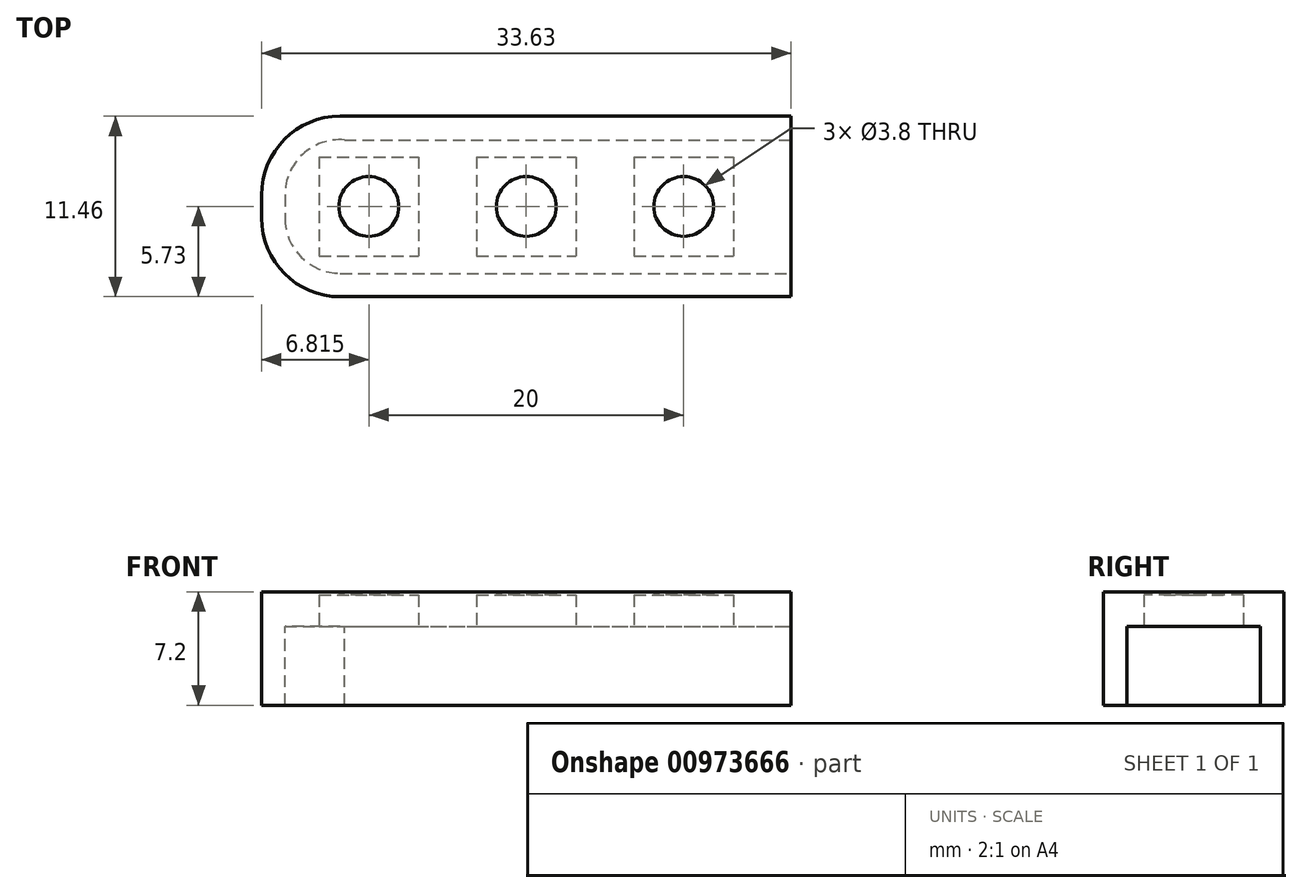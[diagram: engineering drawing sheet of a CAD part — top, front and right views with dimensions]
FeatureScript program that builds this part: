
annotation { "Feature Type Name" : "Feature", "Feature Type Description" : "" }
export const myFeature = defineFeature(function(context is Context, id is Id, definition is map)
    precondition{}
    {
        {
            var Q0;
            Q0=qCreatedBy(makeId("Top.planeOp"),FACE);
            var sketch = newSketch(context, id + "F0", { "sketchPlane" : qUnion([Q0])});
            skLineSegment(sketch, "E0.bottom", {"start": v(-8.24, 3.15) * mm, "end": v(-1.94, 3.15) * mm});
            skLineSegment(sketch, "E0.top", {"start": v(-8.24, -3.15) * mm, "end": v(-1.94, -3.15) * mm});
            skLineSegment(sketch, "E0.left", {"start": v(-8.24, 3.15) * mm, "end": v(-8.24, -3.15) * mm});
            skLineSegment(sketch, "E0.right", {"start": v(-1.94, 3.15) * mm, "end": v(-1.94, -3.15) * mm});
            skPoint(sketch, "E0.middle", {"position": v(-5.09, 0) * mm});
            skLineSegment(sketch, "E1.bottom", {"start": v(1.76, 3.15) * mm, "end": v(8.06, 3.15) * mm});
            skLineSegment(sketch, "E1.top", {"start": v(1.76, -3.15) * mm, "end": v(8.06, -3.15) * mm});
            skLineSegment(sketch, "E1.left", {"start": v(1.76, 3.15) * mm, "end": v(1.76, -3.15) * mm});
            skLineSegment(sketch, "E1.right", {"start": v(8.06, 3.15) * mm, "end": v(8.06, -3.15) * mm});
            skPoint(sketch, "E1.middle", {"position": v(4.91, 0) * mm});
            skLineSegment(sketch, "E2.bottom", {"start": v(11.76, 3.15) * mm, "end": v(18.06, 3.15) * mm});
            skLineSegment(sketch, "E2.top", {"start": v(11.76, -3.15) * mm, "end": v(18.06, -3.15) * mm});
            skLineSegment(sketch, "E2.left", {"start": v(11.76, 3.15) * mm, "end": v(11.76, -3.15) * mm});
            skLineSegment(sketch, "E2.right", {"start": v(18.06, 3.15) * mm, "end": v(18.06, -3.15) * mm});
            skPoint(sketch, "E2.middle", {"position": v(14.91, 0) * mm});
            skLineSegment(sketch, "E3.bottom", {"start": v(-6.9, 5.73) * mm, "end": v(21.73, 5.73) * mm});
            skLineSegment(sketch, "E3.top", {"start": v(-6.9, -5.73) * mm, "end": v(21.73, -5.73) * mm});
            skLineSegment(sketch, "E3.left", {"start": v(-11.9, 0.73) * mm, "end": v(-11.9, -0.73) * mm});
            skLineSegment(sketch, "E3.right", {"start": v(21.73, 5.73) * mm, "end": v(21.73, -5.73) * mm});
            skPoint(sketch, "E4.visualSharp", {"position": v(-11.9, -5.73) * mm});
            skArc(sketch, "E4.filletArc", {"start": v(-11.9, -0.73) * mm, "mid": v(-10.44, -4.27) * mm, "end": v(-6.9, -5.73) * mm});
            skPoint(sketch, "E5.visualSharp", {"position": v(-11.9, 5.73) * mm});
            skArc(sketch, "E5.filletArc", {"start": v(-6.9, 5.73) * mm, "mid": v(-10.44, 4.27) * mm, "end": v(-11.9, 0.73) * mm});
            skSolve(sketch);
        }
        {
            var Q0;
            Q0 = qSketchRegion(id + "F0", true);
            extrude(context, id + "F1", {"entities" : qUnion([Q0]), "depth" : 2 * mm, "offsetDistance" : 25 * mm});
        }
        {
            var Q0;
            Q0=makeQuery(id+"F1.opExtrude","CAP_FACE",FACE,{"disambiguationData":[OSD([sQuery(id+"F0.wireOp",EDGE,"E0.bottom"),sQuery(id+"F0.wireOp",EDGE,"E0.top"),sQuery(id+"F0.wireOp",EDGE,"E0.left"),sQuery(id+"F0.wireOp",EDGE,"E0.right"),sQuery(id+"F0.wireOp",EDGE,"E1.bottom"),sQuery(id+"F0.wireOp",EDGE,"E1.top"),sQuery(id+"F0.wireOp",EDGE,"E1.left"),sQuery(id+"F0.wireOp",EDGE,"E1.right"),sQuery(id+"F0.wireOp",EDGE,"E2.bottom"),sQuery(id+"F0.wireOp",EDGE,"E2.top"),sQuery(id+"F0.wireOp",EDGE,"E2.left"),sQuery(id+"F0.wireOp",EDGE,"E2.right"),sQuery(id+"F0.wireOp",EDGE,"E3.bottom"),sQuery(id+"F0.wireOp",EDGE,"E3.top"),sQuery(id+"F0.wireOp",EDGE,"E3.left"),sQuery(id+"F0.wireOp",EDGE,"E3.right")])],"isStart":true});
            var sketch = newSketch(context, id + "F2", { "sketchPlane" : qUnion([Q0])});
            skLineSegment(sketch, "E6.bottom", {"start": v(-6.9, 5.73) * mm, "end": v(21.73, 5.73) * mm});
            skLineSegment(sketch, "E6.top", {"start": v(-6.9, 4.24) * mm, "end": v(21.73, 4.24) * mm});
            skLineSegment(sketch, "E6.right", {"start": v(21.73, 5.73) * mm, "end": v(21.73, 4.24) * mm});
            skLineSegment(sketch, "E7.bottom", {"start": v(-6.9, -5.73) * mm, "end": v(21.73, -5.73) * mm});
            skLineSegment(sketch, "E7.top", {"start": v(-6.64, -4.23) * mm, "end": v(21.73, -4.23) * mm});
            skLineSegment(sketch, "E7.right", {"start": v(21.73, -5.73) * mm, "end": v(21.73, -4.23) * mm});
            skLineSegment(sketch, "E8.bottom", {"start": v(-6.64, -4.23) * mm, "end": v(-5.4, -4.23) * mm});
            skLineSegment(sketch, "E8.top", {"start": v(-6.9, 4.24) * mm, "end": v(-5.4, 4.24) * mm});
            skArc(sketch, "E9.0", {"start": v(-11.9, 0.73) * mm, "mid": v(-10.44, 4.27) * mm, "end": v(-6.9, 5.73) * mm});
            skLineSegment(sketch, "E9.1", {"start": v(-11.9, -0.73) * mm, "end": v(-11.9, 0.73) * mm});
            skArc(sketch, "E9.2", {"start": v(-6.9, -5.73) * mm, "mid": v(-10.44, -4.27) * mm, "end": v(-11.9, -0.73) * mm});
            skPoint(sketch, "E9.3", {"position": v(-11.9, 0) * mm});
            skArc(sketch, "E10.0", {"start": v(-10.41, 0.73) * mm, "mid": v(-9.39, 3.22) * mm, "end": v(-6.9, 4.24) * mm});
            skLineSegment(sketch, "E10.1", {"start": v(-10.41, -0.73) * mm, "end": v(-10.41, 0.73) * mm});
            skArc(sketch, "E10.2", {"start": v(-6.64, -4.23) * mm, "mid": v(-9.3, -3.3) * mm, "end": v(-10.41, -0.73) * mm});
            skPoint(sketch, "E11", {"position": v(-5.09, 0) * mm});
            skPoint(sketch, "E11.positionSnap0", {"position": v(-5.09, 3.15) * mm});
            skPoint(sketch, "E12", {"position": v(4.91, 0) * mm});
            skPoint(sketch, "E12.positionSnap0", {"position": v(4.91, 3.15) * mm});
            skPoint(sketch, "E12.positionSnap1", {"position": v(8.06, 0) * mm});
            skPoint(sketch, "E13", {"position": v(14.91, 0) * mm});
            skPoint(sketch, "E13.positionSnap0", {"position": v(14.91, 3.15) * mm});
            skSolve(sketch);
        }
        {
            var Q0;
            Q0=makeQuery(id+"F2.imprint","IMPRINT",FACE,{"disambiguationData":[TD([[makeQuery(id+"F2.imprint","IMPRINT",EDGE,{"derivedFrom":sQuery(id+"F2.wireOp",EDGE,"E6.bottom")}),-1.0]])]});
            extrude(context, id + "F3", {"entities" : qUnion([Q0]), "operationType" : NewBodyOperationType.ADD, "depth" : 5 * mm, "offsetDistance" : 25 * mm});
        }
        {
            var Q0;
            Q0=makeQuery(id+"F1.opExtrude","CAP_FACE",FACE,{"disambiguationData":[OSD([sQuery(id+"F0.wireOp",EDGE,"E0.bottom"),sQuery(id+"F0.wireOp",EDGE,"E0.top"),sQuery(id+"F0.wireOp",EDGE,"E0.left"),sQuery(id+"F0.wireOp",EDGE,"E0.right"),sQuery(id+"F0.wireOp",EDGE,"E1.bottom"),sQuery(id+"F0.wireOp",EDGE,"E1.top"),sQuery(id+"F0.wireOp",EDGE,"E1.left"),sQuery(id+"F0.wireOp",EDGE,"E1.right"),sQuery(id+"F0.wireOp",EDGE,"E2.bottom"),sQuery(id+"F0.wireOp",EDGE,"E2.top"),sQuery(id+"F0.wireOp",EDGE,"E2.left"),sQuery(id+"F0.wireOp",EDGE,"E2.right"),sQuery(id+"F0.wireOp",EDGE,"E3.bottom"),sQuery(id+"F0.wireOp",EDGE,"E3.top"),sQuery(id+"F0.wireOp",EDGE,"E3.left"),sQuery(id+"F0.wireOp",EDGE,"E3.right"),sQuery(id+"F0.wireOp",EDGE,"E4.filletArc"),sQuery(id+"F0.wireOp",EDGE,"E5.filletArc")])],"isStart":false});
            var sketch = newSketch(context, id + "F4", { "sketchPlane" : qUnion([Q0])});
            skLineSegment(sketch, "E14.0", {"start": v(-6.9, -5.73) * mm, "end": v(21.73, -5.73) * mm});
            skArc(sketch, "E14.1", {"start": v(-11.9, -0.73) * mm, "mid": v(-10.44, -4.27) * mm, "end": v(-6.9, -5.73) * mm});
            skLineSegment(sketch, "E14.2", {"start": v(-11.9, 0.73) * mm, "end": v(-11.9, -0.73) * mm});
            skArc(sketch, "E14.3", {"start": v(-6.9, 5.73) * mm, "mid": v(-10.44, 4.27) * mm, "end": v(-11.9, 0.73) * mm});
            skLineSegment(sketch, "E14.4", {"start": v(-6.9, 5.73) * mm, "end": v(21.73, 5.73) * mm});
            skLineSegment(sketch, "E14.5", {"start": v(21.73, 5.73) * mm, "end": v(21.73, -5.73) * mm});
            skPoint(sketch, "E14.6", {"position": v(-11.9, 0) * mm});
            skCircle(sketch, "E15", {"center": v(-5.09, 0) * mm, "radius": 1.9 * mm});
            skPoint(sketch, "E15.centerSnap0", {"position": v(-1.94, 0) * mm});
            skPoint(sketch, "E15.centerSnap1", {"position": v(-5.09, -3.15) * mm});
            skCircle(sketch, "E16", {"center": v(4.91, 0) * mm, "radius": 1.9 * mm});
            skPoint(sketch, "E16.centerSnap0", {"position": v(4.91, -3.15) * mm});
            skCircle(sketch, "E17", {"center": v(14.91, 0) * mm, "radius": 1.9 * mm});
            skPoint(sketch, "E17.centerSnap0", {"position": v(11.76, 0) * mm});
            skPoint(sketch, "E17.centerSnap1", {"position": v(14.91, -3.15) * mm});
            skSolve(sketch);
        }
        {
            var Q0;
            Q0 = qSketchRegion(id + "F4", true);
            extrude(context, id + "F5", {"entities" : qUnion([Q0]), "operationType" : NewBodyOperationType.ADD, "depth" : 0.2 * mm, "offsetDistance" : 25 * mm});
        }
    });
